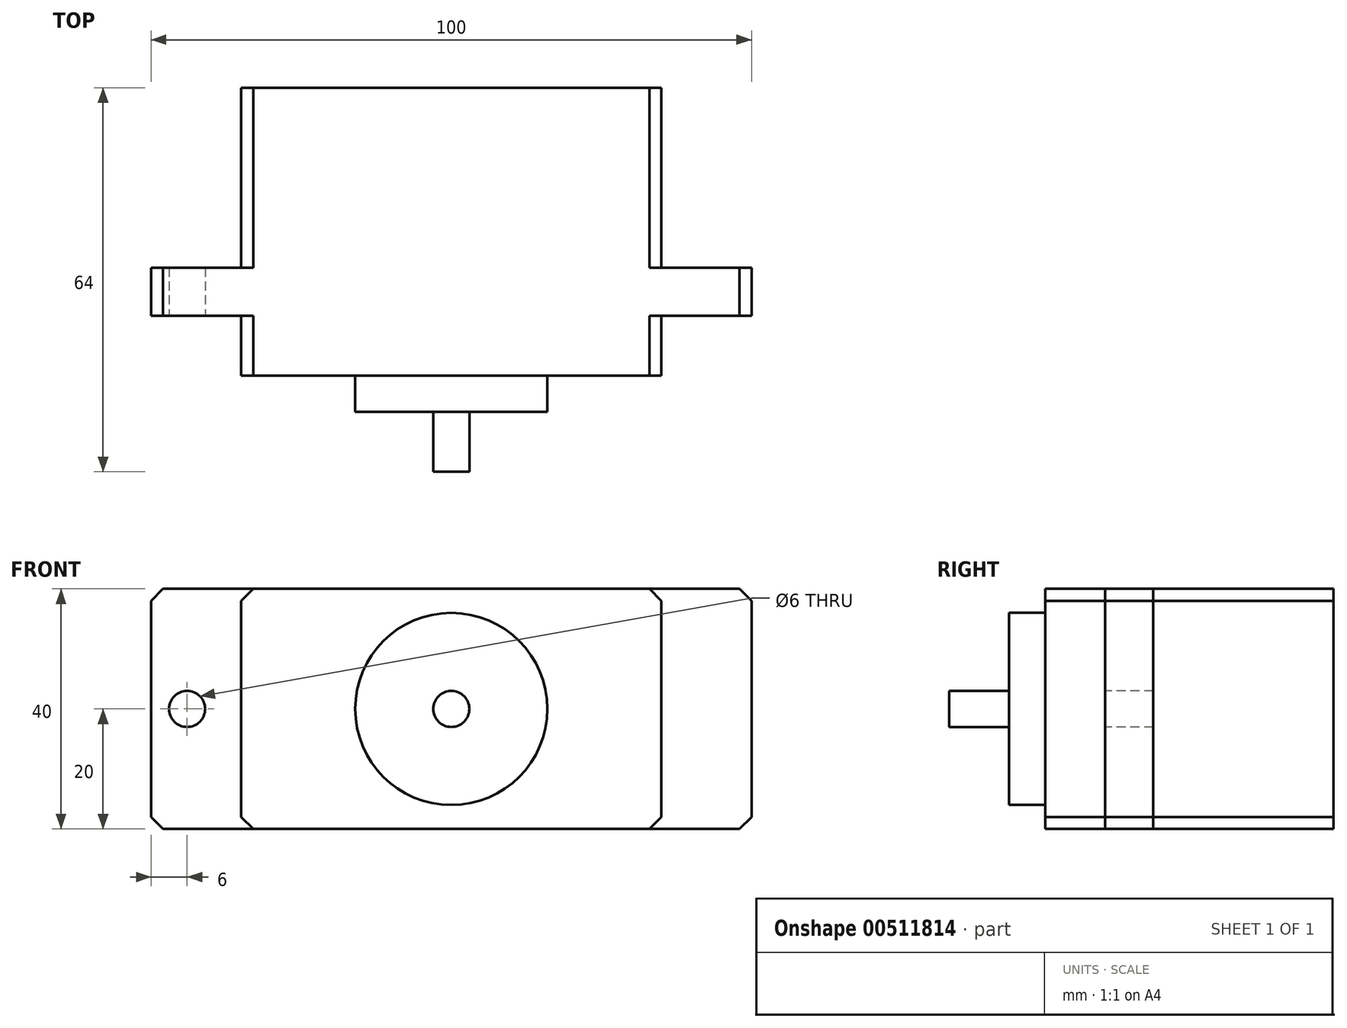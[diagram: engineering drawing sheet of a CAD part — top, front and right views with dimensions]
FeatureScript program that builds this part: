
annotation { "Feature Type Name" : "Feature", "Feature Type Description" : "" }
export const myFeature = defineFeature(function(context is Context, id is Id, definition is map)
    precondition{}
    {
        {
            var Q0;
            Q0=qCreatedBy(makeId("Top.planeOp"),FACE);
            var sketch = newSketch(context, id + "F0", { "sketchPlane" : qUnion([Q0])});
            skLineSegment(sketch, "E0", {"start": v(0, 38.91) * mm, "end": v(0, -49) * mm, "construction": true});
            skLineSegment(sketch, "E1", {"start": v(-50, -8) * mm, "end": v(-35, -8) * mm});
            skLineSegment(sketch, "E2", {"start": v(-35, -8) * mm, "end": v(-35, -18) * mm});
            skLineSegment(sketch, "E3", {"start": v(-35, -18) * mm, "end": v(0, -18) * mm});
            skLineSegment(sketch, "E4", {"start": v(-50, -8) * mm, "end": v(-50, 0) * mm});
            skLineSegment(sketch, "E5", {"start": v(-50, 0) * mm, "end": v(-35, 0) * mm});
            skLineSegment(sketch, "E6", {"start": v(-35, 0) * mm, "end": v(-35, 30) * mm});
            skLineSegment(sketch, "E7", {"start": v(-35, 30) * mm, "end": v(0, 30) * mm});
            skLineSegment(sketch, "E8.MirrorCS", {"start": v(50, -8) * mm, "end": v(35, -8) * mm});
            skLineSegment(sketch, "E9.MirrorCS", {"start": v(35, 30) * mm, "end": v(0, 30) * mm});
            skLineSegment(sketch, "E10.MirrorCS", {"start": v(35, 0) * mm, "end": v(35, 30) * mm});
            skLineSegment(sketch, "E11.MirrorCS", {"start": v(50, -8) * mm, "end": v(50, 0) * mm});
            skLineSegment(sketch, "E12.MirrorCS", {"start": v(35, -8) * mm, "end": v(35, -18) * mm});
            skLineSegment(sketch, "E13.MirrorCS", {"start": v(35, -18) * mm, "end": v(0, -18) * mm});
            skLineSegment(sketch, "E14.MirrorCS", {"start": v(50, 0) * mm, "end": v(35, 0) * mm});
            skSolve(sketch);
        }
        {
            var Q0;
            Q0=makeQuery(id+"F0.imprint","IMPRINT",FACE,{"disambiguationData":[TD([[makeQuery(id+"F0.imprint","IMPRINT",EDGE,{"derivedFrom":sQuery(id+"F0.wireOp",EDGE,"E1")}),1.0]])]});
            extrude(context, id + "F1", {"entities" : qUnion([Q0]), "depth" : 40 * mm});
        }
        {
            var Q0;
            Q0=makeQuery(id+"F1.opExtrude","CAP_EDGE",EDGE,{"disambiguationData":[OSD([sQuery(id+"F0.wireOp",EDGE,"E10.MirrorCS")])],"isStart":false});
            var Q1;
            Q1=makeQuery(id+"F1.opExtrude","CAP_EDGE",EDGE,{"disambiguationData":[OSD([sQuery(id+"F0.wireOp",EDGE,"E12.MirrorCS")])],"isStart":false});
            var Q2;
            Q2=makeQuery(id+"F1.opExtrude","CAP_EDGE",EDGE,{"disambiguationData":[OSD([sQuery(id+"F0.wireOp",EDGE,"E11.MirrorCS")])],"isStart":false});
            var Q3;
            Q3=makeQuery(id+"F1.opExtrude","CAP_EDGE",EDGE,{"disambiguationData":[OSD([sQuery(id+"F0.wireOp",EDGE,"E12.MirrorCS")])],"isStart":true});
            var Q4;
            Q4=makeQuery(id+"F1.opExtrude","CAP_EDGE",EDGE,{"disambiguationData":[OSD([sQuery(id+"F0.wireOp",EDGE,"E11.MirrorCS")])],"isStart":true});
            var Q5;
            Q5=makeQuery(id+"F1.opExtrude","CAP_EDGE",EDGE,{"disambiguationData":[OSD([sQuery(id+"F0.wireOp",EDGE,"E10.MirrorCS")])],"isStart":true});
            var Q6;
            Q6=makeQuery(id+"F1.opExtrude","CAP_EDGE",EDGE,{"disambiguationData":[OSD([sQuery(id+"F0.wireOp",EDGE,"E6")])],"isStart":false});
            var Q7;
            Q7=makeQuery(id+"F1.opExtrude","CAP_EDGE",EDGE,{"disambiguationData":[OSD([sQuery(id+"F0.wireOp",EDGE,"E2")])],"isStart":false});
            var Q8;
            Q8=makeQuery(id+"F1.opExtrude","CAP_EDGE",EDGE,{"disambiguationData":[OSD([sQuery(id+"F0.wireOp",EDGE,"E4")])],"isStart":false});
            var Q9;
            Q9=makeQuery(id+"F1.opExtrude","CAP_EDGE",EDGE,{"disambiguationData":[OSD([sQuery(id+"F0.wireOp",EDGE,"E6")])],"isStart":true});
            var Q10;
            Q10=makeQuery(id+"F1.opExtrude","CAP_EDGE",EDGE,{"disambiguationData":[OSD([sQuery(id+"F0.wireOp",EDGE,"E4")])],"isStart":true});
            var Q11;
            Q11=makeQuery(id+"F1.opExtrude","CAP_EDGE",EDGE,{"disambiguationData":[OSD([sQuery(id+"F0.wireOp",EDGE,"E2")])],"isStart":true});
            chamfer(context, id + "F2", {"entities" : qUnion([Q0, Q1, Q2, Q3, Q4, Q5, Q6, Q7, Q8, Q9, Q10, Q11]), "width" : 2 * mm, "tangentPropagation" : true});
        }
        {
            var Q0;
            Q0=makeQuery(id+"F1.opExtrude","SWEPT_FACE",FACE,{"disambiguationData":[OSD([sQuery(id+"F0.wireOp",EDGE,"E3"),sQuery(id+"F0.wireOp",EDGE,"E13.MirrorCS")])]});
            var sketch = newSketch(context, id + "F3", { "sketchPlane" : qUnion([Q0])});
            skLineSegment(sketch, "E15", {"start": v(-57.18, 20) * mm, "end": v(59.81, 20) * mm, "construction": true});
            skCircle(sketch, "E16", {"center": v(0, 20) * mm, "radius": 16 * mm});
            skSolve(sketch);
        }
        {
            var Q0;
            Q0 = qSketchRegion(id + "F3", true);
            extrude(context, id + "F4", {"entities" : qUnion([Q0]), "operationType" : NewBodyOperationType.ADD, "depth" : 6 * mm});
        }
        {
            var Q0;
            Q0=makeQuery(id+"F4.opExtrude","CAP_FACE",FACE,{"disambiguationData":[OSD([sQuery(id+"F3.wireOp",EDGE,"E16")])],"isStart":false});
            var sketch = newSketch(context, id + "F5", { "sketchPlane" : qUnion([Q0])});
            skCircle(sketch, "E17", {"center": v(0, 20) * mm, "radius": 3 * mm});
            skSolve(sketch);
        }
        {
            var Q0;
            Q0 = qSketchRegion(id + "F5", true);
            extrude(context, id + "F6", {"entities" : qUnion([Q0]), "operationType" : NewBodyOperationType.ADD, "depth" : 10 * mm});
        }
        {
            var Q0;
            Q0=makeQuery(id+"F1.opExtrude","SWEPT_FACE",FACE,{"disambiguationData":[OSD([sQuery(id+"F0.wireOp",EDGE,"E1")])]});
            var sketch = newSketch(context, id + "F7", { "sketchPlane" : qUnion([Q0])});
            skCircle(sketch, "E18", {"center": v(-44, 20) * mm, "radius": 3 * mm});
            skLineSegment(sketch, "E19.0", {"start": v(-50, 38) * mm, "end": v(-50, 2) * mm});
            skCircle(sketch, "E20.MirrorC", {"center": v(44, 20) * mm, "radius": 3 * mm});
            skSolve(sketch);
        }
        {
            var Q0;
            Q0=makeQuery(id+"F7.imprint","IMPRINT",FACE,{"disambiguationData":[TD([[makeQuery(id+"F7.imprint","IMPRINT",EDGE,{"derivedFrom":sQuery(id+"F7.wireOp",EDGE,"E18")}),1.0]])]});
            var Q1;
            Q1=makeQuery(id+"F7.imprint","IMPRINT",FACE,{"disambiguationData":[TD([[makeQuery(id+"F7.imprint","IMPRINT",EDGE,{"derivedFrom":sQuery(id+"F7.wireOp",EDGE,"E20.MirrorC")}),-1.0]])]});
            extrude(context, id + "F8", {"entities" : qUnion([Q0, Q1]), "operationType" : NewBodyOperationType.REMOVE, "oppositeDirection" : true, "depth" : 25 * mm});
        }
    });
